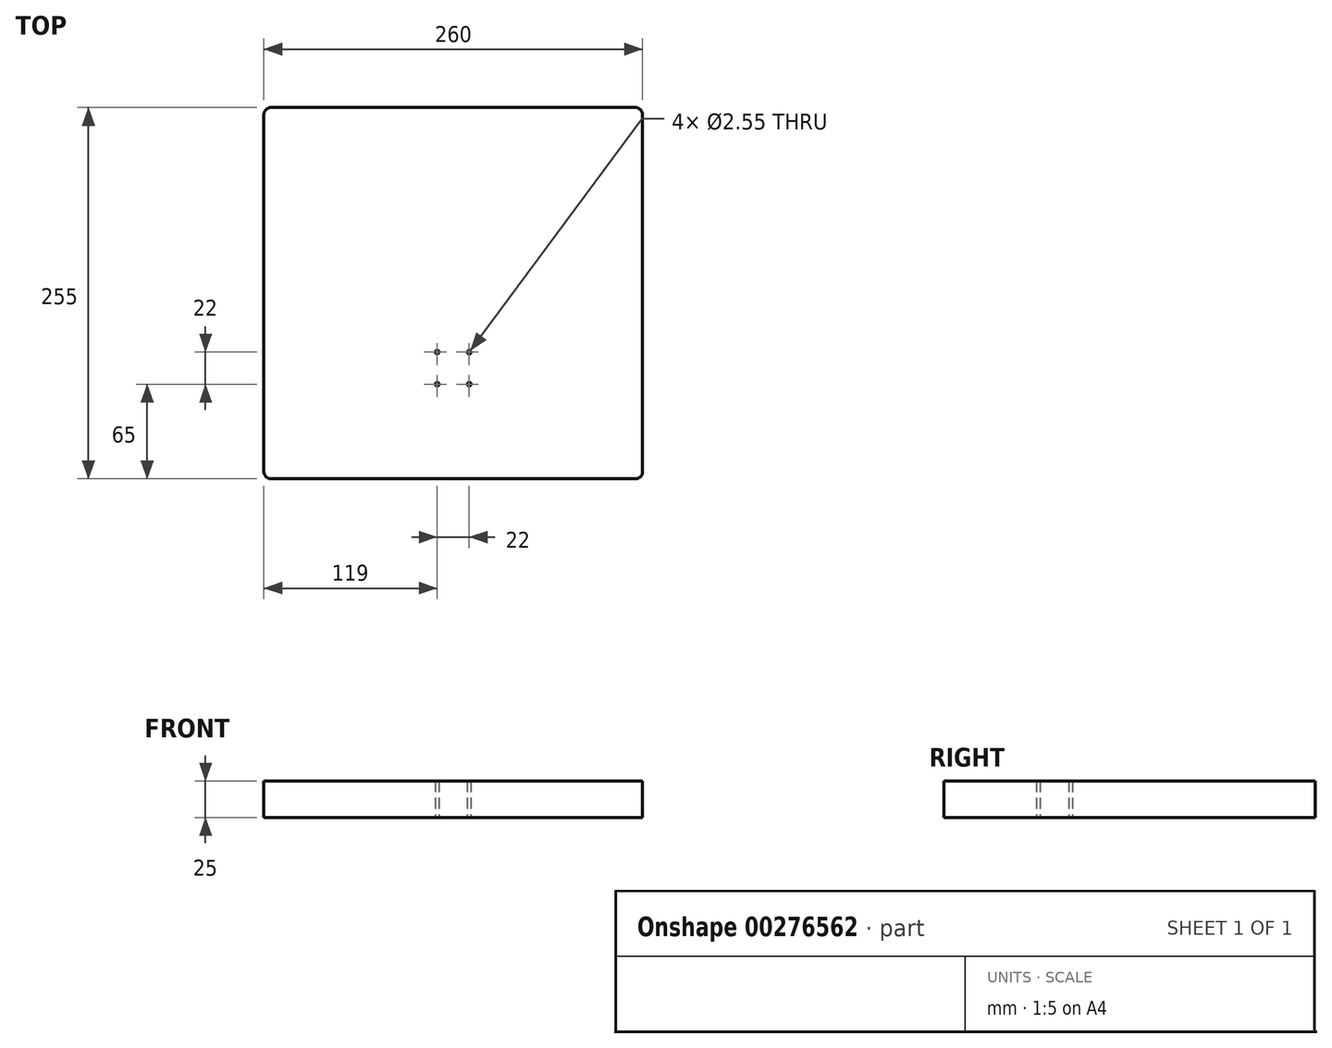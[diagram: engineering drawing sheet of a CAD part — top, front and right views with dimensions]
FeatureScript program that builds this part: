
annotation { "Feature Type Name" : "Feature", "Feature Type Description" : "" }
export const myFeature = defineFeature(function(context is Context, id is Id, definition is map)
    precondition{}
    {
        {
            var Q0;
            Q0=qCreatedBy(makeId("Top.planeOp"),FACE);
            var sketch = newSketch(context, id + "F0", { "sketchPlane" : qUnion([Q0])});
            skLineSegment(sketch, "E0.bottom", {"start": v(130, -127.5) * mm, "end": v(-130, -127.5) * mm});
            skLineSegment(sketch, "E0.top", {"start": v(130, 127.5) * mm, "end": v(-130, 127.5) * mm});
            skLineSegment(sketch, "E0.left", {"start": v(130, -127.5) * mm, "end": v(130, 127.5) * mm});
            skLineSegment(sketch, "E0.right", {"start": v(-130, -127.5) * mm, "end": v(-130, 127.5) * mm});
            skPoint(sketch, "E0.middle", {"position": v(0, 0) * mm});
            skSolve(sketch);
        }
        {
            var Q0;
            Q0 = qSketchRegion(id + "F0", true);
            extrude(context, id + "F1", {"entities" : qUnion([Q0]), "depth" : 25 * mm, "offsetDistance" : 25 * mm});
        }
        {
            var Q0;
            Q0=makeQuery(id+"F1.opExtrude","CAP_FACE",FACE,{"disambiguationData":[OSD([sQuery(id+"F0.wireOp",EDGE,"E0.bottom"),sQuery(id+"F0.wireOp",EDGE,"E0.top"),sQuery(id+"F0.wireOp",EDGE,"E0.left"),sQuery(id+"F0.wireOp",EDGE,"E0.right")])],"isStart":false});
            var sketch = newSketch(context, id + "F2", { "sketchPlane" : qUnion([Q0])});
            skPoint(sketch, "E1", {"position": v(-11, -40.5) * mm});
            skPoint(sketch, "E2", {"position": v(11, -40.5) * mm});
            skPoint(sketch, "E3", {"position": v(-11, -62.5) * mm});
            skPoint(sketch, "E4", {"position": v(11, -62.5) * mm});
            skSolve(sketch);
        }
        {
            var Q0;
            Q0=sQuery(id+"F2.wireOp",VERTEX,"E1");
            var Q1;
            Q1=sQuery(id+"F2.wireOp",VERTEX,"E2");
            var Q2;
            Q2=sQuery(id+"F2.wireOp",VERTEX,"E4");
            var Q3;
            Q3=sQuery(id+"F2.wireOp",VERTEX,"E3");
            var Q4;
            Q4=makeQuery(id+"F1.opExtrude","SWEPT_BODY",BODY,{"disambiguationData":[OSD([sQuery(id+"F0.wireOp",EDGE,"E0.bottom"),sQuery(id+"F0.wireOp",EDGE,"E0.top"),sQuery(id+"F0.wireOp",EDGE,"E0.left"),sQuery(id+"F0.wireOp",EDGE,"E0.right")])]});
            hole(context, id + "F3", {"style" : HoleStyle.SIMPLE, "endStyle" : HoleEndStyle.THROUGH, "holeDiameter" : 2.55 * mm, "majorDiameter" : 5 * mm, "tappedDepth" : 12 * mm, "tapClearance" : 3, "locations" : qUnion([Q0, Q1, Q2, Q3]), "scope" : qUnion([Q4])});
        }
        {
            var Q0;
            Q0=makeQuery(id+"F1.opExtrude","SWEPT_EDGE",EDGE,{"disambiguationData":[OSD([sQuery(id+"F0.wireOp",EDGE,"E0.bottom"),sQuery(id+"F0.wireOp",EDGE,"E0.right")])]});
            var Q1;
            Q1=makeQuery(id+"F1.opExtrude","SWEPT_EDGE",EDGE,{"disambiguationData":[OSD([sQuery(id+"F0.wireOp",EDGE,"E0.bottom"),sQuery(id+"F0.wireOp",EDGE,"E0.left")])]});
            var Q2;
            Q2=makeQuery(id+"F1.opExtrude","SWEPT_EDGE",EDGE,{"disambiguationData":[OSD([sQuery(id+"F0.wireOp",EDGE,"E0.top"),sQuery(id+"F0.wireOp",EDGE,"E0.left")])]});
            var Q3;
            Q3=makeQuery(id+"F1.opExtrude","SWEPT_EDGE",EDGE,{"disambiguationData":[OSD([sQuery(id+"F0.wireOp",EDGE,"E0.top"),sQuery(id+"F0.wireOp",EDGE,"E0.right")])]});
            fillet(context, id + "F4", {"entities" : qUnion([Q0, Q1, Q2, Q3]), "radius" : 5 * mm, "tangentPropagation" : true, "allowEdgeOverflow" : false});
        }
    });
